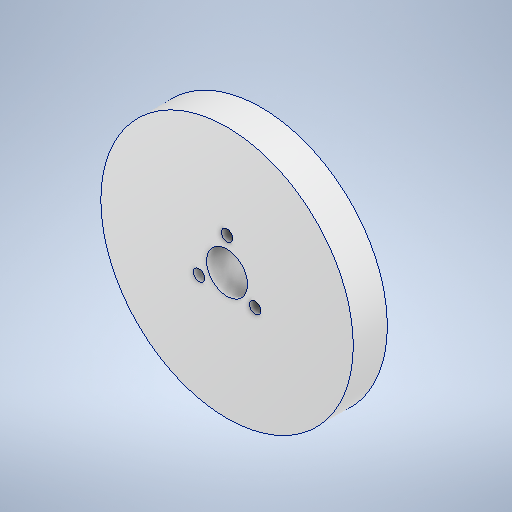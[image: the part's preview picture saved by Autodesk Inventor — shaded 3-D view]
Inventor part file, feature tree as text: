
AUTODESK INVENTOR PART (.ipt)
format: ipt  version: 2025.2 (Build 292293000, 293)  size: 261,632 bytes
history: native  units: in
note: dims shown in document units (in); Inventor stores cm internally (conversion verified against a paired STEP export)
features: sketch x5, extrude x4
ambient origin geometry x8: Origin, YZ Plane, XZ Plane, XY Plane, X Axis, Y Axis, Z Axis, Center Point
bodies: Solid1 (feature_tree)
feature tree (9):
  extrude  "Extrusion1"  Depth=0.3937in TaperAngle=0.0deg
  extrude  "Extrusion3"  Depth=1.3386in
  extrude  "Extrusion4"  Depth=0.2362in
  extrude  "Extrusion6"  Depth=0.2756in
  sketch  "Sketch1"  dims[d0=2.9134in d1=0.3937in d2=0.0in]
  sketch  "Sketch4"  dims[d7=0.2362in d8=0.0in d9=1.1811in]
  sketch  "Sketch6"  dims[d10=0.2756in d11=0.0in d16=0.748in]
  sketch  "Sketch8"  dims[d17=0.1299in d18=1.1811in d20=360.0deg d22=0.0in d23=0.0in d24=0.4724in]
  sketch  "Sketch Circular Pattern1"  dims[d5=0.315in d6=1.3386in]
